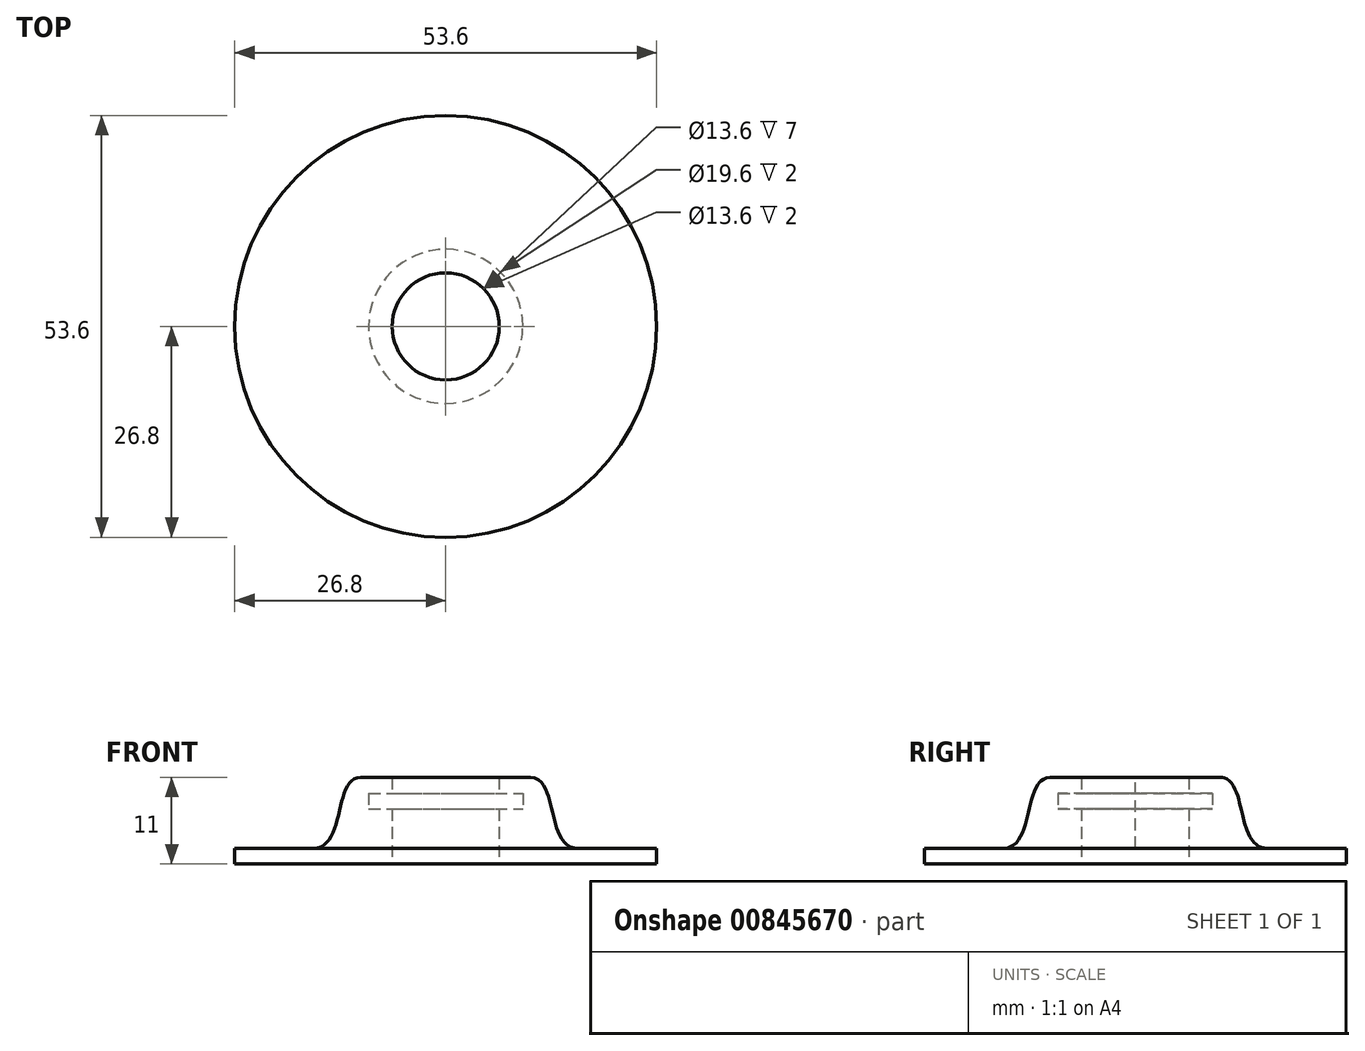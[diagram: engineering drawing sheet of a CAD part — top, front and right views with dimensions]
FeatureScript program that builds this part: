
annotation { "Feature Type Name" : "Feature", "Feature Type Description" : "" }
export const myFeature = defineFeature(function(context is Context, id is Id, definition is map)
    precondition{}
    {
        {
            var Q0;
            Q0=qCreatedBy(makeId("Front.planeOp"),FACE);
            var sketch = newSketch(context, id + "F0", { "sketchPlane" : qUnion([Q0])});
            skLineSegment(sketch, "E0.bottom", {"start": v(-6.8, 0) * mm, "end": v(-16.8, 0) * mm});
            skLineSegment(sketch, "E0.top", {"start": v(-6.8, 2) * mm, "end": v(-16.8, 2) * mm});
            skLineSegment(sketch, "E0.left", {"start": v(-6.8, 0) * mm, "end": v(-6.8, 2) * mm});
            skLineSegment(sketch, "E0.right", {"start": v(-16.8, 0) * mm, "end": v(-16.8, 2) * mm});
            skLineSegment(sketch, "E1.bottom", {"start": v(-6.8, 2) * mm, "end": v(-10.8, 2) * mm});
            skLineSegment(sketch, "E1.top", {"start": v(-6.8, 7) * mm, "end": v(-10.8, 7) * mm});
            skLineSegment(sketch, "E1.left", {"start": v(-6.8, 2) * mm, "end": v(-6.8, 7) * mm});
            skLineSegment(sketch, "E1.right", {"start": v(-10.8, 2) * mm, "end": v(-10.8, 7) * mm});
            skLineSegment(sketch, "E2.bottom", {"start": v(-10.8, 7) * mm, "end": v(-9.8, 7) * mm});
            skLineSegment(sketch, "E2.top", {"start": v(-10.8, 9) * mm, "end": v(-9.8, 9) * mm});
            skLineSegment(sketch, "E2.left", {"start": v(-10.8, 7) * mm, "end": v(-10.8, 9) * mm});
            skLineSegment(sketch, "E2.right", {"start": v(-9.8, 7) * mm, "end": v(-9.8, 9) * mm});
            skLineSegment(sketch, "E3.bottom", {"start": v(-10.8, 9) * mm, "end": v(-6.8, 9) * mm});
            skLineSegment(sketch, "E3.top", {"start": v(-10.8, 11) * mm, "end": v(-6.8, 11) * mm});
            skLineSegment(sketch, "E3.left", {"start": v(-10.8, 9) * mm, "end": v(-10.8, 11) * mm});
            skLineSegment(sketch, "E3.right", {"start": v(-6.8, 9) * mm, "end": v(-6.8, 11) * mm});
            skFitSpline(sketch, "E4", {"points": [v(-16.8, 2) * mm, v(-10.8, 11) * mm], "startDerivative": vector(12.51, 0) * mm, "endDerivative": vector(10.69, 0) * mm});
            skLineSegment(sketch, "E5.bottom", {"start": v(-16.8, 0) * mm, "end": v(-26.8, 0) * mm});
            skLineSegment(sketch, "E5.top", {"start": v(-16.8, 2) * mm, "end": v(-26.8, 2) * mm});
            skLineSegment(sketch, "E5.right", {"start": v(-26.8, 0) * mm, "end": v(-26.8, 2) * mm});
            skLineSegment(sketch, "E6", {"start": v(0, 0) * mm, "end": v(0, 5.4) * mm});
            skSolve(sketch);
        }
        {
            var Q0;
            Q0=makeQuery(id+"F0.imprint","IMPRINT",FACE,{"disambiguationData":[TD([[makeQuery(id+"F0.imprint","IMPRINT",EDGE,{"derivedFrom":sQuery(id+"F0.wireOp",EDGE,"E2.top")}),1.0]])]});
            var Q1;
            Q1=makeQuery(id+"F0.imprint","IMPRINT",FACE,{"disambiguationData":[TD([[makeQuery(id+"F0.imprint","IMPRINT",EDGE,{"derivedFrom":sQuery(id+"F0.wireOp",EDGE,"E2.top")}),-1.0]])]});
            var Q2;
            {var subQ0=sQuery(id+"F0.wireOp",EDGE,"E1.right");Q2=makeQuery(id+"F0.imprint","IMPRINT",FACE,{"disambiguationData":[TD([[makeQuery(id+"F0.imprint","IMPRINT",EDGE,{"derivedFrom":subQ0}),1.0]])]});}
            var Q3;
            {var subQ2=sQuery(id+"F0.wireOp",EDGE,"E1.left");Q3=makeQuery(id+"F0.imprint","IMPRINT",FACE,{"disambiguationData":[TD([[makeQuery(id+"F0.imprint","IMPRINT",EDGE,{"derivedFrom":subQ2}),1.0]])]});}
            var Q4;
            Q4=makeQuery(id+"F0.imprint","IMPRINT",FACE,{"disambiguationData":[TD([[makeQuery(id+"F0.imprint","IMPRINT",EDGE,{"derivedFrom":sQuery(id+"F0.wireOp",EDGE,"E0.bottom")}),-1.0]])]});
            var Q5;
            Q5=makeQuery(id+"F0.imprint","IMPRINT",FACE,{"disambiguationData":[TD([[makeQuery(id+"F0.imprint","IMPRINT",EDGE,{"derivedFrom":sQuery(id+"F0.wireOp",EDGE,"E0.right")}),1.0]])]});
            var Q6;
            Q6=sQuery(id+"F0.wireOp",EDGE,"E6");
            revolve(context, id + "F1", {"surfaceOperationType" : NewSurfaceOperationType.NEW, "entities" : qUnion([Q0, Q1, Q2, Q3, Q4, Q5]), "axis" : qUnion([Q6]), "revolveType" : RevolveType.FULL});
        }
    });
